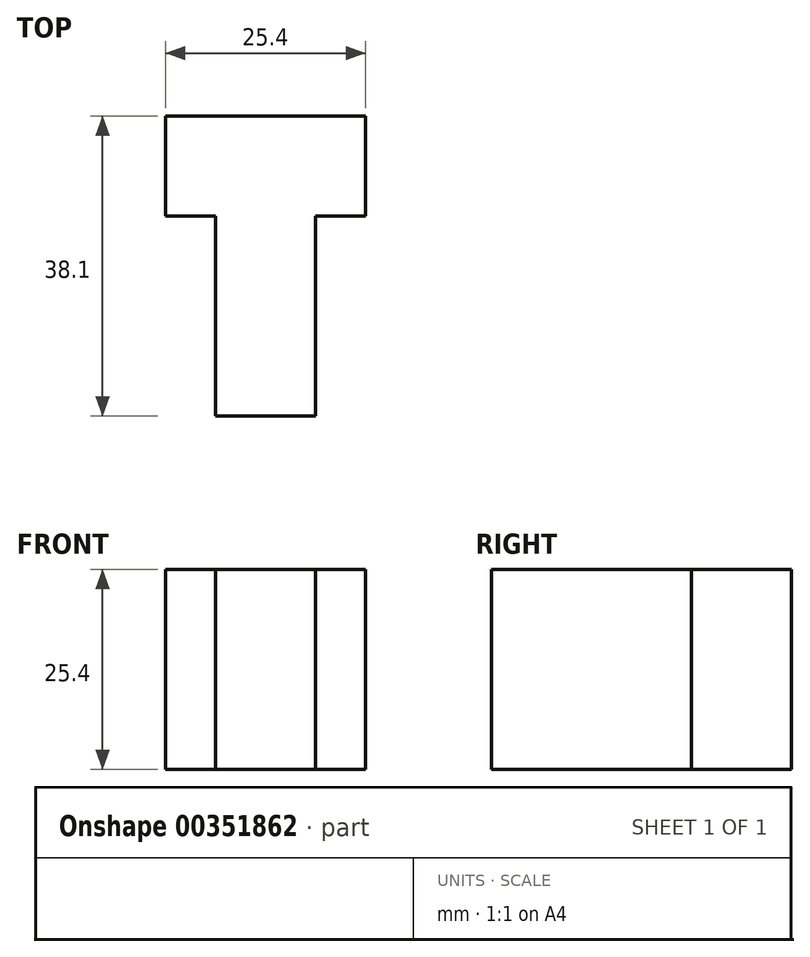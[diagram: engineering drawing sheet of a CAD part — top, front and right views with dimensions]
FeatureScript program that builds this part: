
annotation { "Feature Type Name" : "Feature", "Feature Type Description" : "" }
export const myFeature = defineFeature(function(context is Context, id is Id, definition is map)
    precondition{}
    {
        {
            var Q0;
            Q0=qCreatedBy(makeId("Top.planeOp"),FACE);
            var sketch = newSketch(context, id + "F0", { "sketchPlane" : qUnion([Q0])});
            skLineSegment(sketch, "E0", {"start": v(-25.4, 38.1) * mm, "end": v(0, 38.1) * mm});
            skLineSegment(sketch, "E1", {"start": v(-25.4, 38.1) * mm, "end": v(-25.4, 25.4) * mm});
            skLineSegment(sketch, "E2", {"start": v(-25.4, 25.4) * mm, "end": v(-19.05, 25.4) * mm});
            skLineSegment(sketch, "E3", {"start": v(-19.05, 25.4) * mm, "end": v(-19.05, 0) * mm});
            skLineSegment(sketch, "E4", {"start": v(-19.05, 0) * mm, "end": v(-6.35, 0) * mm});
            skLineSegment(sketch, "E5", {"start": v(-6.35, 25.4) * mm, "end": v(-6.35, 0) * mm});
            skLineSegment(sketch, "E6", {"start": v(-6.35, 25.4) * mm, "end": v(0, 25.4) * mm});
            skLineSegment(sketch, "E7", {"start": v(0, 25.4) * mm, "end": v(0, 38.1) * mm});
            skSolve(sketch);
        }
        {
            var Q0;
            Q0=makeQuery(id+"F0.imprint","IMPRINT",FACE,{"disambiguationData":[TD([[makeQuery(id+"F0.imprint","IMPRINT",EDGE,{"derivedFrom":sQuery(id+"F0.wireOp",EDGE,"E0")}),-1.0]])]});
            extrude(context, id + "F1", {"entities" : qUnion([Q0]), "depth" : 25.4 * mm});
        }
    });
